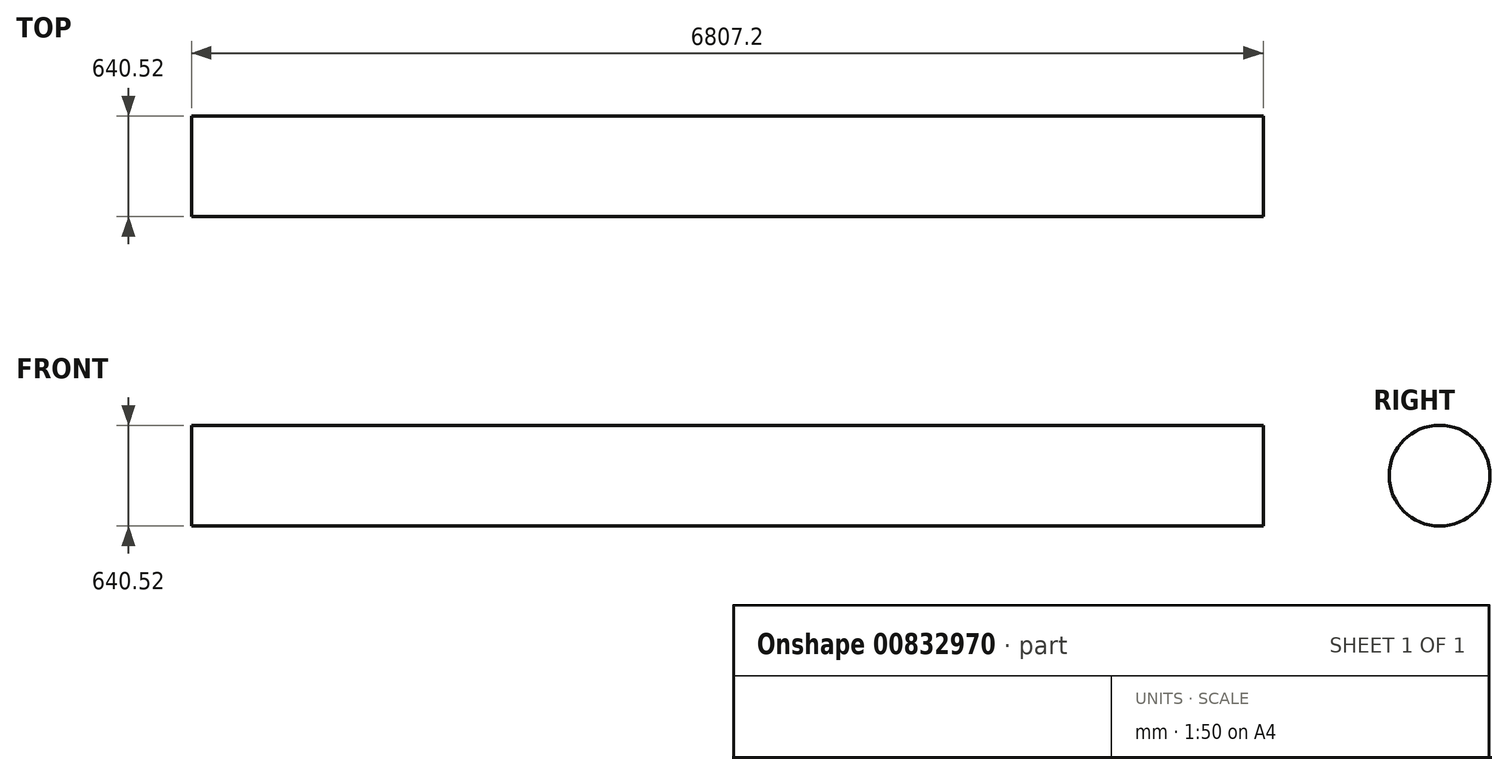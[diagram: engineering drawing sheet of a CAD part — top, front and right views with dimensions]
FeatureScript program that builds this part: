
annotation { "Feature Type Name" : "Feature", "Feature Type Description" : "" }
export const myFeature = defineFeature(function(context is Context, id is Id, definition is map)
    precondition{}
    {
        {
            var Q0;
            Q0=qCreatedBy(makeId("Right.planeOp"),FACE);
            var sketch = newSketch(context, id + "F0", { "sketchPlane" : qUnion([Q0])});
            skCircle(sketch, "E0", {"center": v(0, 0) * mm, "radius": 320.26 * mm});
            skSolve(sketch);
        }
        {
            var Q0;
            Q0=makeQuery(id+"F0.imprint","IMPRINT",FACE,{"disambiguationData":[TD([[makeQuery(id+"F0.imprint","IMPRINT",EDGE,{"derivedFrom":sQuery(id+"F0.wireOp",EDGE,"E0")}),1.0]])]});
            extrude(context, id + "F1", {"entities" : qUnion([Q0]), "depth" : 6807.2 * mm, "offsetDistance" : 25.4 * mm});
        }
    });
